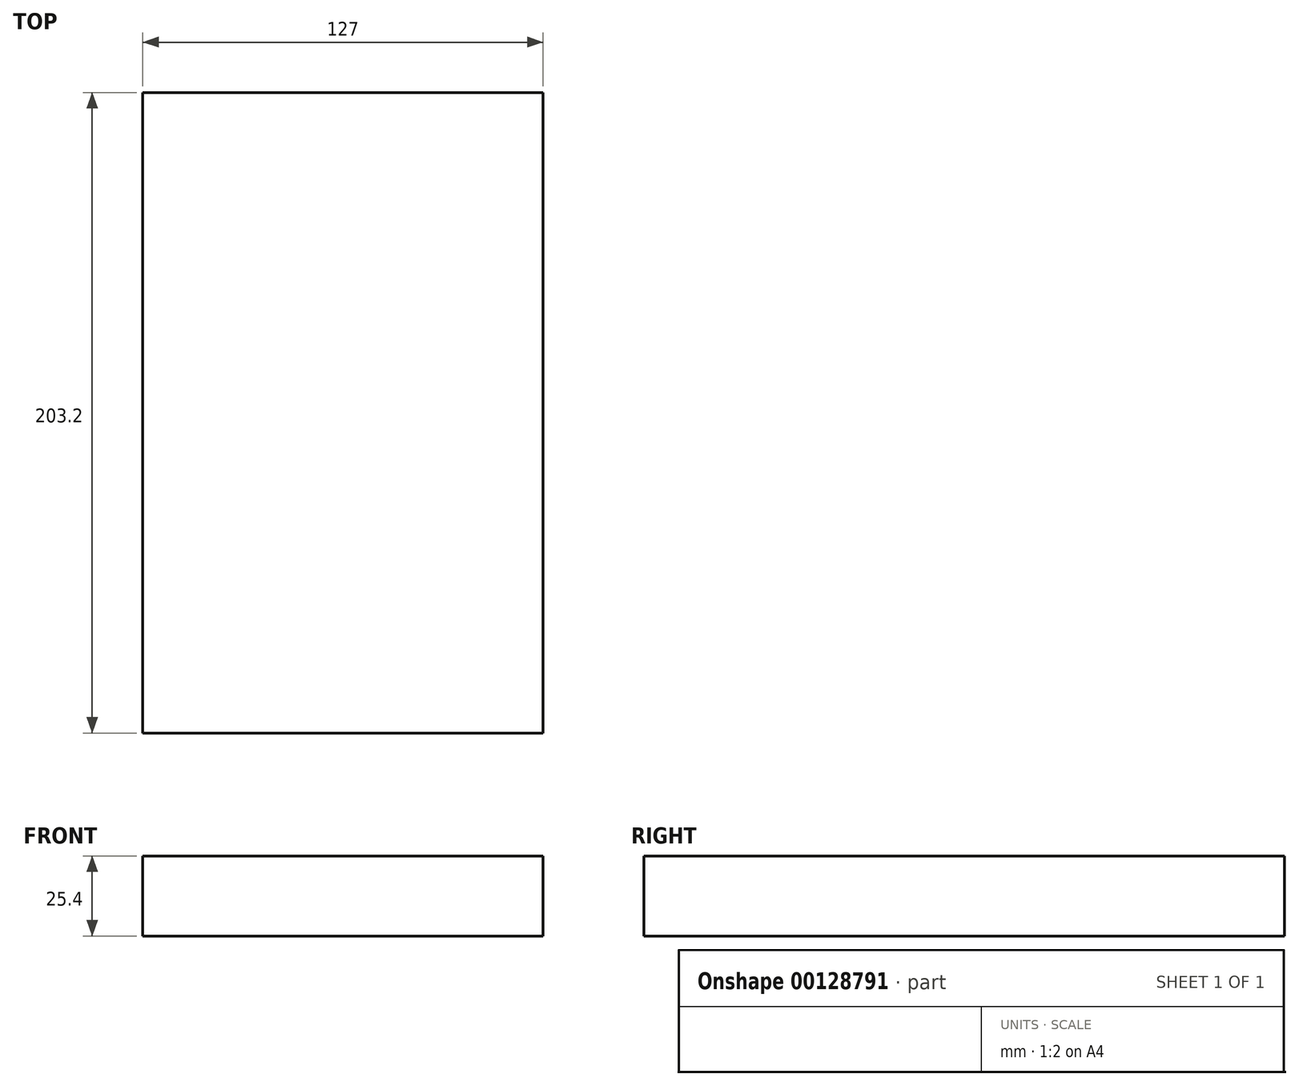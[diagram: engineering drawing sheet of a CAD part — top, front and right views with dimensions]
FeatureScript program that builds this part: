
annotation { "Feature Type Name" : "Feature", "Feature Type Description" : "" }
export const myFeature = defineFeature(function(context is Context, id is Id, definition is map)
    precondition{}
    {
        {
            var Q0;
            Q0=qCreatedBy(makeId("Right.planeOp"),FACE);
            cPlane(context, id + "F0", {"entities" : qUnion([Q0]), "cplaneType" : CPlaneType.OFFSET, "offset" : 63.5 * mm, "width" : 152.4 * mm, "height" : 152.4 * mm});
        }
        {
            var Q0;
            Q0=qCreatedBy(makeId("Right.planeOp"),FACE);
            cPlane(context, id + "F1", {"entities" : qUnion([Q0]), "cplaneType" : CPlaneType.OFFSET, "offset" : 63.5 * mm, "oppositeDirection" : true, "width" : 152.4 * mm, "height" : 152.4 * mm});
        }
        {
            var Q0;
            Q0=qCreatedBy(makeId("Top.planeOp"),FACE);
            var sketch = newSketch(context, id + "F2", { "sketchPlane" : qUnion([Q0])});
            skLineSegment(sketch, "E0.bottom", {"start": v(-63.5, 0) * mm, "end": v(63.5, 0) * mm});
            skLineSegment(sketch, "E0.top", {"start": v(-63.5, -203.2) * mm, "end": v(63.5, -203.2) * mm});
            skLineSegment(sketch, "E0.left", {"start": v(-63.5, 0) * mm, "end": v(-63.5, -203.2) * mm});
            skLineSegment(sketch, "E0.right", {"start": v(63.5, 0) * mm, "end": v(63.5, -203.2) * mm});
            skSolve(sketch);
        }
        {
            var Q0;
            Q0=makeQuery(id+"F2.imprint","IMPRINT",FACE,{"disambiguationData":[TD([[makeQuery(id+"F2.imprint","IMPRINT",EDGE,{"derivedFrom":sQuery(id+"F2.wireOp",EDGE,"E0.bottom")}),-1.0]])]});
            extrude(context, id + "F3", {"entities" : qUnion([Q0]), "oppositeDirection" : true, "depth" : 25.4 * mm});
        }
    });
